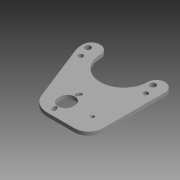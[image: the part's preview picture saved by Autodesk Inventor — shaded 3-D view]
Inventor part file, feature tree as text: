
AUTODESK INVENTOR PART (.ipt)
format: ipt  version: 2015 (Build 190159000, 159)  size: 146,432 bytes
history: native  units: mm
features: reference x7, extrude x1, sketch x1
ambient origin geometry x8: Origin, YZ Plane, XZ Plane, XY Plane, X Axis, Y Axis, Z Axis, Center Point
bodies: Solid1 (feature_tree)
feature tree (9):
  extrude  "Extrusion1"  Depth=12.0mm
  sketch  "Sketch1"  dims[d2=6.0mm d3=12.0mm d4=3.0mm d5=3.0mm d10=0.872665mm d12=8.683013mm d14=0.872665mm d15=3.0mm d16=0.0mm d21=12.5mm d22=0.872665mm d23=4.0mm d24=4.0mm d25=5.0mm d26=5.0mm]
  reference  "Reference1"
  reference  "Reference2"
  reference  "Reference3"
  reference  "Reference4"
  reference  "Reference5"
  reference  "Reference6"
  reference  "Reference7"
